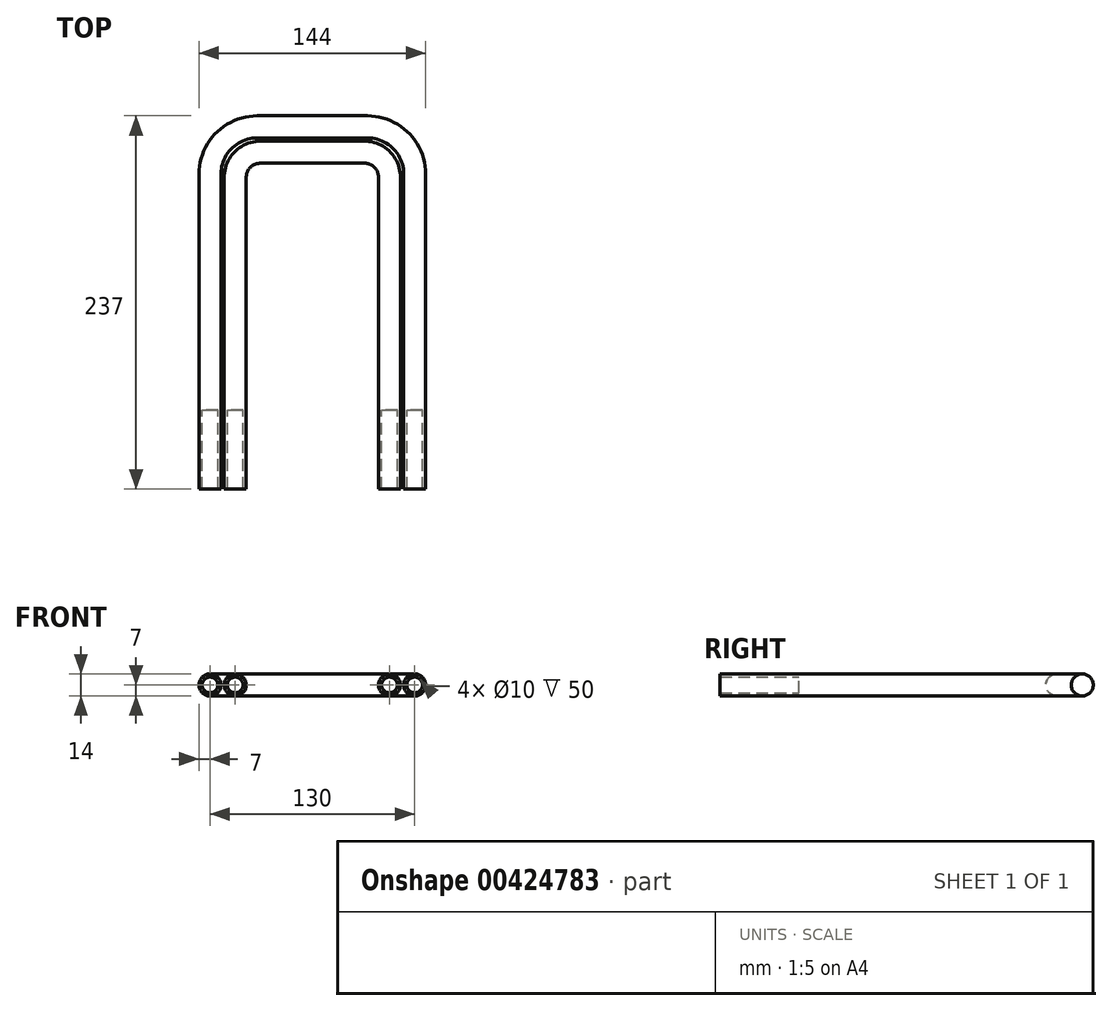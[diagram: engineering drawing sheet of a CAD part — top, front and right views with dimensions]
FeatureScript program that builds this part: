
annotation { "Feature Type Name" : "Feature", "Feature Type Description" : "" }
export const myFeature = defineFeature(function(context is Context, id is Id, definition is map)
    precondition{}
    {
        {
            var Q0;
            Q0=qCreatedBy(makeId("Top.planeOp"),FACE);
            var sketch = newSketch(context, id + "F0", { "sketchPlane" : qUnion([Q0])});
            skLineSegment(sketch, "E0", {"start": v(0, 0) * mm, "end": v(0, 150) * mm});
            skLineSegment(sketch, "E1", {"start": v(30, 180) * mm, "end": v(100, 180) * mm});
            skLineSegment(sketch, "E2", {"start": v(130, 150) * mm, "end": v(130, 0) * mm});
            skPoint(sketch, "E3.visualSharp", {"position": v(0, 180) * mm});
            skArc(sketch, "E3.filletArc", {"start": v(30, 180) * mm, "mid": v(8.79, 171.21) * mm, "end": v(0, 150) * mm});
            skPoint(sketch, "E4.visualSharp", {"position": v(130, 180) * mm});
            skArc(sketch, "E4.filletArc", {"start": v(130, 150) * mm, "mid": v(121.21, 171.21) * mm, "end": v(100, 180) * mm});
            skSolve(sketch);
        }
        {
            var Q0;
            Q0=qCreatedBy(makeId("Front.planeOp"),FACE);
            var sketch = newSketch(context, id + "F1", { "sketchPlane" : qUnion([Q0])});
            skCircle(sketch, "E5", {"center": v(0, 0) * mm, "radius": 7 * mm});
            skSolve(sketch);
        }
        {
            var Q0;
            Q0=qSketchRegion(id+"F1",true);
            var Q1;
            Q1=qConstructionFilter(qBodyType(qCreatedBy(id+"F0",EDGE),BodyType.WIRE),ConstructionObject.NO);
            sweep(context, id + "F2", {"profiles" : qUnion([Q0]), "path" : qUnion([Q1])});
        }
        {
            var Q0;
            Q0=makeQuery(id+"F2.opSweep","CAP_FACE",FACE,{"disambiguationData":[OSD([sQuery(id+"F0.wireOp",VERTEX,"E2.end"),sQuery(id+"F1.wireOp",EDGE,"E5")])],"isStart":false});
            var sketch = newSketch(context, id + "F3", { "sketchPlane" : qUnion([Q0])});
            skCircle(sketch, "E6", {"center": v(0, 0) * mm, "radius": 5 * mm});
            skCircle(sketch, "E7", {"center": v(130, 0) * mm, "radius": 5 * mm});
            skCircle(sketch, "E8", {"center": v(0, 0) * mm, "radius": 7 * mm});
            skCircle(sketch, "E9", {"center": v(130, 0) * mm, "radius": 7 * mm});
            skSolve(sketch);
        }
        {
            var Q0;
            Q0=qSketchRegion(id+"F3",true);
            extrude(context, id + "F4", {"entities" : qUnion([Q0]), "operationType" : NewBodyOperationType.ADD, "depth" : 50 * mm});
        }
        {
            var Q0;
            Q0=qCreatedBy(makeId("Front.planeOp"),FACE);
            var sketch = newSketch(context, id + "F5", { "sketchPlane" : qUnion([Q0])});
            skCircle(sketch, "E10", {"center": v(16, 0) * mm, "radius": 7 * mm});
            skSolve(sketch);
        }
        {
            var Q0;
            Q0=qCreatedBy(makeId("Top.planeOp"),FACE);
            var sketch = newSketch(context, id + "F6", { "sketchPlane" : qUnion([Q0])});
            skLineSegment(sketch, "E11", {"start": v(16, 0) * mm, "end": v(16, 147.92) * mm});
            skLineSegment(sketch, "E12", {"start": v(114, 147.98) * mm, "end": v(114, 0) * mm});
            skLineSegment(sketch, "E13", {"start": v(31.98, 163.92) * mm, "end": v(97.98, 163.98) * mm});
            skPoint(sketch, "E14.visualSharp", {"position": v(16, 163.9) * mm});
            skArc(sketch, "E14.filletArc", {"start": v(31.98, 163.92) * mm, "mid": v(20.68, 159.22) * mm, "end": v(16, 147.92) * mm});
            skPoint(sketch, "E15.visualSharp", {"position": v(114, 164) * mm});
            skArc(sketch, "E15.filletArc", {"start": v(114, 147.98) * mm, "mid": v(109.3, 159.3) * mm, "end": v(97.98, 163.98) * mm});
            skSolve(sketch);
        }
        {
            var Q0;
            Q0=makeQuery(id+"F5.imprint","IMPRINT",FACE,{"disambiguationData":[TD([[makeQuery(id+"F5.imprint","IMPRINT",EDGE,{"derivedFrom":sQuery(id+"F5.wireOp",EDGE,"E10")}),1.0]])]});
            var Q1;
            Q1=qConstructionFilter(qBodyType(qCreatedBy(id+"F6",EDGE),BodyType.WIRE),ConstructionObject.NO);
            sweep(context, id + "F7", {"operationType" : NewBodyOperationType.ADD, "profiles" : qUnion([Q0]), "path" : qUnion([Q1])});
        }
        {
            var Q0;
            Q0=makeQuery(id+"F7.opSweep","CAP_FACE",FACE,{"disambiguationData":[OSD([sQuery(id+"F5.wireOp",EDGE,"E10"),sQuery(id+"F6.wireOp",VERTEX,"E11.start")])],"isStart":true});
            var sketch = newSketch(context, id + "F8", { "sketchPlane" : qUnion([Q0])});
            skCircle(sketch, "E16", {"center": v(16, 0) * mm, "radius": 5 * mm});
            skCircle(sketch, "E17", {"center": v(114, 0) * mm, "radius": 5 * mm});
            skCircle(sketch, "E18", {"center": v(16, 0) * mm, "radius": 7 * mm});
            skCircle(sketch, "E19", {"center": v(114, 0) * mm, "radius": 7 * mm});
            skSolve(sketch);
        }
        {
            var Q0;
            Q0=qSketchRegion(id+"F8",true);
            extrude(context, id + "F9", {"entities" : qUnion([Q0]), "operationType" : NewBodyOperationType.ADD, "depth" : 50 * mm});
        }
    });
